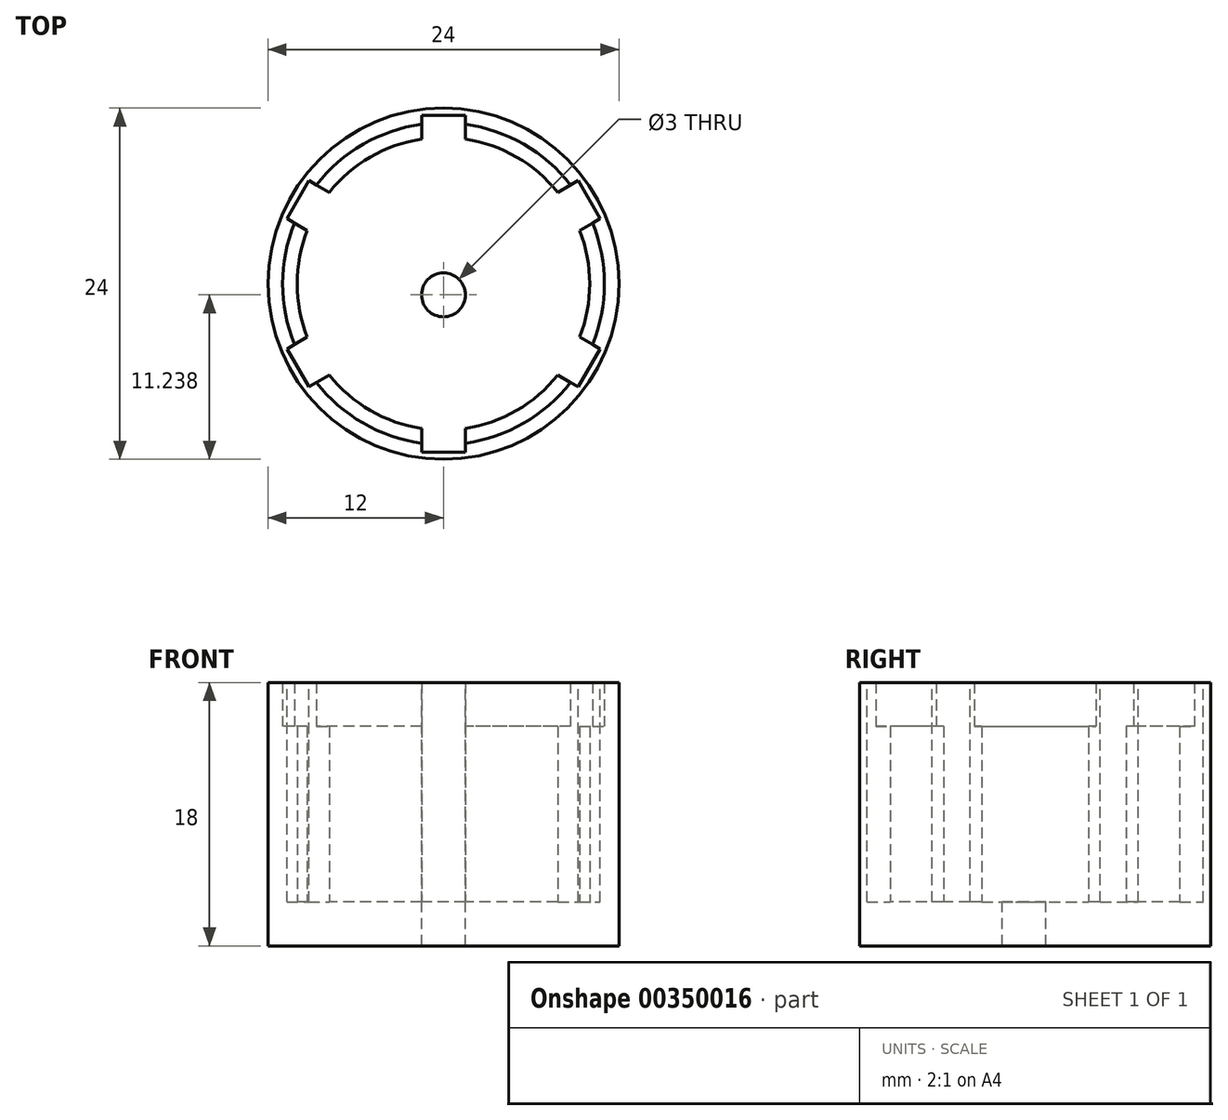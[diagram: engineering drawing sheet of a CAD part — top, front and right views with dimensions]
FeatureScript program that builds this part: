
annotation { "Feature Type Name" : "Feature", "Feature Type Description" : "" }
export const myFeature = defineFeature(function(context is Context, id is Id, definition is map)
    precondition{}
    {
        {
            var Q0;
            Q0=qCreatedBy(makeId("Top.planeOp"),FACE);
            var sketch = newSketch(context, id + "F0", { "sketchPlane" : qUnion([Q0])});
            skCircle(sketch, "E0", {"center": v(0, 0) * mm, "radius": 12 * mm});
            skCircle(sketch, "E1", {"center": v(0, 0) * mm, "radius": 11 * mm});
            skCircle(sketch, "E2", {"center": v(0, 0) * mm, "radius": 10 * mm});
            skSolve(sketch);
        }
        {
            var Q0;
            Q0=makeQuery(id+"F0.imprint","IMPRINT",FACE,{"disambiguationData":[TD([[makeQuery(id+"F0.imprint","IMPRINT",EDGE,{"derivedFrom":sQuery(id+"F0.wireOp",EDGE,"E2")}),1.0]])]});
            var Q1;
            Q1=sQuery(id+"F0.wireOp",EDGE,"E2");
            var Q2;
            Q2=sQuery(id+"F0.wireOp",EDGE,"E1");
            var Q3;
            Q3=sQuery(id+"F0.wireOp",EDGE,"E0");
            extrude(context, id + "F1", {"entities" : qUnion([Q0]), "surfaceEntities" : qUnion([Q1, Q2, Q3]), "depth" : 3 * mm});
        }
        {
            var Q0;
            Q0=makeQuery(id+"F0.imprint","IMPRINT",FACE,{"disambiguationData":[TD([[makeQuery(id+"F0.imprint","IMPRINT",EDGE,{"derivedFrom":sQuery(id+"F0.wireOp",EDGE,"E1")}),1.0]])]});
            extrude(context, id + "F2", {"entities" : qUnion([Q0]), "operationType" : NewBodyOperationType.ADD, "depth" : 15 * mm});
        }
        {
            var Q0;
            Q0=makeQuery(id+"F0.imprint","IMPRINT",FACE,{"disambiguationData":[TD([[makeQuery(id+"F0.imprint","IMPRINT",EDGE,{"derivedFrom":sQuery(id+"F0.wireOp",EDGE,"E0")}),1.0]])]});
            extrude(context, id + "F3", {"entities" : qUnion([Q0]), "operationType" : NewBodyOperationType.ADD, "depth" : 18 * mm});
        }
        {
            var Q0;
            Q0=makeQuery(id+"F1.opExtrude","CAP_FACE",FACE,{"disambiguationData":[OSD([sQuery(id+"F0.wireOp",EDGE,"E2")])],"isStart":false});
            var sketch = newSketch(context, id + "F4", { "sketchPlane" : qUnion([Q0])});
            skCircle(sketch, "E3", {"center": v(0, -0.76) * mm, "radius": 1.5 * mm});
            skSolve(sketch);
        }
        {
            var Q0;
            Q0=makeQuery(id+"F4.imprint","IMPRINT",FACE,{"disambiguationData":[TD([[makeQuery(id+"F4.imprint","IMPRINT",EDGE,{"derivedFrom":sQuery(id+"F4.wireOp",EDGE,"E3")}),1.0]])]});
            var Q1;
            Q1=sQuery(id+"F4.wireOp",EDGE,"E3");
            extrude(context, id + "F5", {"entities" : qUnion([Q0]), "operationType" : NewBodyOperationType.REMOVE, "surfaceEntities" : qUnion([Q1]), "oppositeDirection" : true, "depth" : 3 * mm});
        }
        {
            var Q0;
            Q0=makeQuery(id+"F3.opExtrude","CAP_FACE",FACE,{"disambiguationData":[OSD([sQuery(id+"F0.wireOp",EDGE,"E0"),sQuery(id+"F0.wireOp",EDGE,"E1")])],"isStart":false});
            var sketch = newSketch(context, id + "F6", { "sketchPlane" : qUnion([Q0])});
            skLineSegment(sketch, "E4.bottom", {"start": v(1.5, -11.5) * mm, "end": v(-1.5, -11.5) * mm});
            skLineSegment(sketch, "E4.top", {"start": v(1.5, 11.5) * mm, "end": v(-1.5, 11.5) * mm});
            skLineSegment(sketch, "E4.left", {"start": v(1.5, -11.5) * mm, "end": v(1.5, 11.5) * mm});
            skLineSegment(sketch, "E4.right", {"start": v(-1.5, -11.5) * mm, "end": v(-1.5, 11.5) * mm});
            skPoint(sketch, "E4.middle", {"position": v(0, 0) * mm});
            skLineSegment(sketch, "E5.1.0", {"start": v(-10.7, -4.45) * mm, "end": v(-9.2, -7.05) * mm});
            skLineSegment(sketch, "E5.1.1", {"start": v(10.7, 4.45) * mm, "end": v(-9.2, -7.05) * mm});
            skLineSegment(sketch, "E5.1.2", {"start": v(9.2, 7.05) * mm, "end": v(-10.7, -4.45) * mm});
            skLineSegment(sketch, "E5.1.3", {"start": v(9.2, 7.05) * mm, "end": v(10.7, 4.45) * mm});
            skLineSegment(sketch, "E5.2.0", {"start": v(9.2, -7.05) * mm, "end": v(10.7, -4.45) * mm});
            skLineSegment(sketch, "E5.2.1", {"start": v(-9.2, 7.05) * mm, "end": v(10.7, -4.45) * mm});
            skLineSegment(sketch, "E5.2.2", {"start": v(-10.7, 4.45) * mm, "end": v(9.2, -7.05) * mm});
            skLineSegment(sketch, "E5.2.3", {"start": v(-10.7, 4.45) * mm, "end": v(-9.2, 7.05) * mm});
            skSolve(sketch);
        }
        {
            var Q0;
            {var subQ3=sQuery(id+"F6.wireOp",EDGE,"E5.1.2");var subQ5=sQuery(id+"F6.wireOp",EDGE,"E4.left");var subQ6=makeQuery(id+"F6.imprint","INTERSECT",VERTEX,{"derivedFrom":[subQ5,subQ3]});Q0=makeQuery(id+"F6.imprint","IMPRINT",FACE,{"disambiguationData":[TD([[makeQuery(id+"F6.imprint","IMPRINT",EDGE,{"disambiguationData":[TD([[subQ6,-1.0]])],"derivedFrom":subQ5}),1.0]])]});}
            var Q1;
            {var subQ0=sQuery(id+"F6.wireOp",EDGE,"E4.top");Q1=makeQuery(id+"F6.imprint","IMPRINT",FACE,{"disambiguationData":[TD([[makeQuery(id+"F6.imprint","IMPRINT",EDGE,{"derivedFrom":subQ0}),1.0]])]});}
            var Q2;
            {var subQ0=sQuery(id+"F6.wireOp",EDGE,"E5.2.3");Q2=makeQuery(id+"F6.imprint","IMPRINT",FACE,{"disambiguationData":[TD([[makeQuery(id+"F6.imprint","IMPRINT",EDGE,{"derivedFrom":subQ0}),-1.0]])]});}
            var Q3;
            {var subQ1=sQuery(id+"F6.wireOp",EDGE,"E5.1.2");var subQ6=sQuery(id+"F6.wireOp",EDGE,"E4.right");var subQ9=makeQuery(id+"F6.imprint","INTERSECT",VERTEX,{"derivedFrom":[subQ6,subQ1]});Q3=makeQuery(id+"F6.imprint","IMPRINT",FACE,{"disambiguationData":[TD([[makeQuery(id+"F6.imprint","IMPRINT",EDGE,{"disambiguationData":[TD([[subQ9,-1.0]])],"derivedFrom":subQ6}),1.0]])]});}
            var Q4;
            {var subQ5=sQuery(id+"F6.wireOp",EDGE,"E4.right");var subQ7=sQuery(id+"F6.wireOp",EDGE,"E5.1.1");var subQ8=makeQuery(id+"F6.imprint","INTERSECT",VERTEX,{"derivedFrom":[subQ5,subQ7]});Q4=makeQuery(id+"F6.imprint","IMPRINT",FACE,{"disambiguationData":[TD([[makeQuery(id+"F6.imprint","IMPRINT",EDGE,{"disambiguationData":[TD([[subQ8,-1.0]])],"derivedFrom":subQ5}),1.0]])]});}
            var Q5;
            {var subQ0=sQuery(id+"F6.wireOp",EDGE,"E5.2.2");var subQ1=sQuery(id+"F6.wireOp",EDGE,"E4.left");var subQ2=makeQuery(id+"F6.imprint","INTERSECT",VERTEX,{"derivedFrom":[subQ1,subQ0]});Q5=makeQuery(id+"F6.imprint","IMPRINT",FACE,{"disambiguationData":[TD([[makeQuery(id+"F6.imprint","IMPRINT",EDGE,{"disambiguationData":[TD([[subQ2,1.0]])],"derivedFrom":subQ1}),1.0]])]});}
            var Q6;
            {var subQ0=sQuery(id+"F6.wireOp",EDGE,"E5.2.2");var subQ1=sQuery(id+"F6.wireOp",EDGE,"E4.left");var subQ2=makeQuery(id+"F6.imprint","INTERSECT",VERTEX,{"derivedFrom":[subQ1,subQ0]});Q6=makeQuery(id+"F6.imprint","IMPRINT",FACE,{"disambiguationData":[TD([[makeQuery(id+"F6.imprint","IMPRINT",EDGE,{"disambiguationData":[TD([[subQ2,-1.0]])],"derivedFrom":subQ1}),-1.0]])]});}
            var Q7;
            {var subQ0=sQuery(id+"F6.wireOp",EDGE,"E5.2.1");var subQ1=sQuery(id+"F6.wireOp",EDGE,"E4.left");var subQ2=makeQuery(id+"F6.imprint","INTERSECT",VERTEX,{"derivedFrom":[subQ1,subQ0]});Q7=makeQuery(id+"F6.imprint","IMPRINT",FACE,{"disambiguationData":[TD([[makeQuery(id+"F6.imprint","IMPRINT",EDGE,{"disambiguationData":[TD([[subQ2,-1.0]])],"derivedFrom":subQ1}),-1.0]])]});}
            var Q8;
            {var subQ0=sQuery(id+"F6.wireOp",EDGE,"E5.1.3");Q8=makeQuery(id+"F6.imprint","IMPRINT",FACE,{"disambiguationData":[TD([[makeQuery(id+"F6.imprint","IMPRINT",EDGE,{"derivedFrom":subQ0}),-1.0]])]});}
            var Q9;
            {var subQ0=sQuery(id+"F6.wireOp",EDGE,"E5.2.0");Q9=makeQuery(id+"F6.imprint","IMPRINT",FACE,{"disambiguationData":[TD([[makeQuery(id+"F6.imprint","IMPRINT",EDGE,{"derivedFrom":subQ0}),1.0]])]});}
            var Q10;
            {var subQ0=sQuery(id+"F6.wireOp",EDGE,"E4.bottom");Q10=makeQuery(id+"F6.imprint","IMPRINT",FACE,{"disambiguationData":[TD([[makeQuery(id+"F6.imprint","IMPRINT",EDGE,{"derivedFrom":subQ0}),-1.0]])]});}
            var Q11;
            {var subQ0=sQuery(id+"F6.wireOp",EDGE,"E5.1.0");Q11=makeQuery(id+"F6.imprint","IMPRINT",FACE,{"disambiguationData":[TD([[makeQuery(id+"F6.imprint","IMPRINT",EDGE,{"derivedFrom":subQ0}),1.0]])]});}
            extrude(context, id + "F7", {"entities" : qUnion([Q0, Q1, Q2, Q3, Q4, Q5, Q6, Q7, Q8, Q9, Q10, Q11]), "operationType" : NewBodyOperationType.REMOVE, "oppositeDirection" : true, "depth" : 15 * mm});
        }
    });
